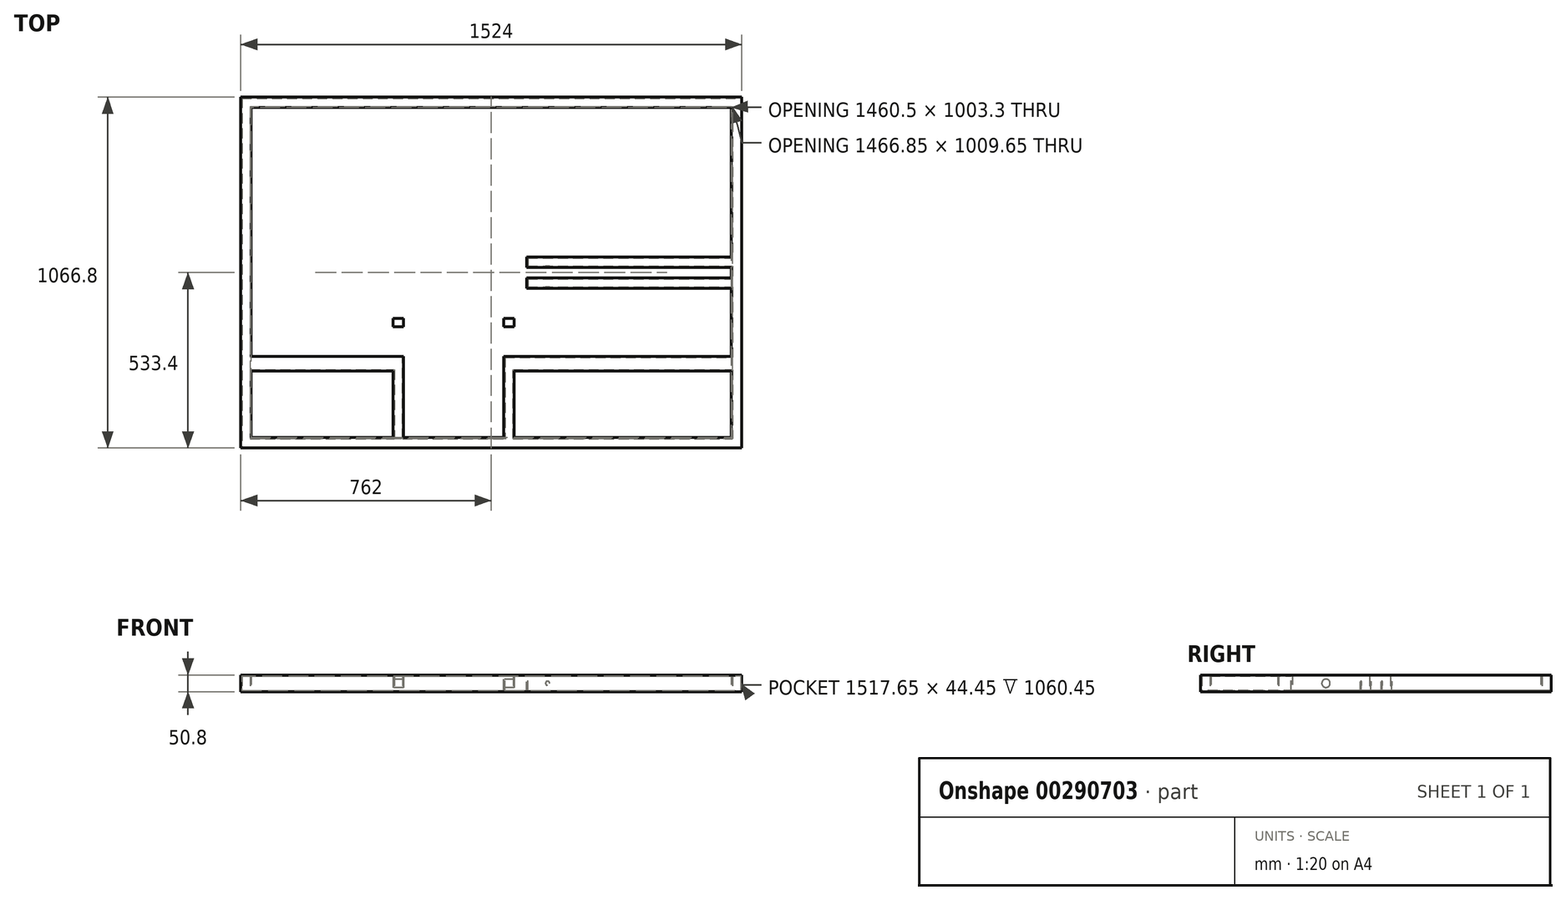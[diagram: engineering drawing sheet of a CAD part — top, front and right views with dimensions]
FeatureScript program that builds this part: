
annotation { "Feature Type Name" : "Feature", "Feature Type Description" : "" }
export const myFeature = defineFeature(function(context is Context, id is Id, definition is map)
    precondition{}
    {
        {
            var Q0;
            Q0=qCreatedBy(makeId("Top.planeOp"),FACE);
            var sketch = newSketch(context, id + "F0", { "sketchPlane" : qUnion([Q0])});
            skLineSegment(sketch, "E0.bottom", {"start": v(0, 0) * mm, "end": v(1524, 0) * mm});
            skLineSegment(sketch, "E0.top", {"start": v(0, -1066.8) * mm, "end": v(1524, -1066.8) * mm});
            skLineSegment(sketch, "E0.left", {"start": v(0, 0) * mm, "end": v(0, -1066.8) * mm});
            skLineSegment(sketch, "E0.right", {"start": v(1524, 0) * mm, "end": v(1524, -1066.8) * mm});
            skLineSegment(sketch, "E1.0", {"start": v(31.75, -31.75) * mm, "end": v(463.55, -31.75) * mm});
            skLineSegment(sketch, "E1.1", {"start": v(31.75, -31.75) * mm, "end": v(31.75, -1035.05) * mm});
            skLineSegment(sketch, "E1.2", {"start": v(31.75, -1035.05) * mm, "end": v(463.55, -1035.05) * mm});
            skLineSegment(sketch, "E1.3", {"start": v(1492.25, -31.75) * mm, "end": v(1492.25, -485.77) * mm});
            skLineSegment(sketch, "E2", {"start": v(463.55, -31.75) * mm, "end": v(463.55, -1035.05) * mm});
            skLineSegment(sketch, "E3", {"start": v(495.3, -1035.05) * mm, "end": v(495.3, -31.75) * mm});
            skLineSegment(sketch, "E4", {"start": v(800.1, -31.75) * mm, "end": v(800.1, -1035.05) * mm});
            skLineSegment(sketch, "E5", {"start": v(831.85, -1035.05) * mm, "end": v(831.85, -581.02) * mm});
            skLineSegment(sketch, "E6.trimOffspring", {"start": v(831.85, -1035.05) * mm, "end": v(1492.25, -1035.05) * mm});
            skLineSegment(sketch, "E7.trimOffspring", {"start": v(495.3, -1035.05) * mm, "end": v(800.1, -1035.05) * mm});
            skLineSegment(sketch, "E8.trimOffspring", {"start": v(495.3, -31.75) * mm, "end": v(800.1, -31.75) * mm});
            skLineSegment(sketch, "E9.trimOffspring", {"start": v(831.85, -31.75) * mm, "end": v(1492.25, -31.75) * mm});
            skLineSegment(sketch, "E10", {"start": v(31.75, -533.4) * mm, "end": v(2205.19, -533.4) * mm, "construction": true});
            skLineSegment(sketch, "E11.bottom", {"start": v(831.85, -517.52) * mm, "end": v(1492.25, -517.52) * mm});
            skLineSegment(sketch, "E11.top", {"start": v(831.85, -485.77) * mm, "end": v(1492.25, -485.77) * mm});
            skLineSegment(sketch, "E12.trimOffspring", {"start": v(831.85, -485.77) * mm, "end": v(831.85, -31.75) * mm});
            skLineSegment(sketch, "E13.trimOffspring", {"start": v(1492.25, -517.52) * mm, "end": v(1492.25, -549.27) * mm});
            skLineSegment(sketch, "E14.MirrorCS", {"start": v(831.85, -549.27) * mm, "end": v(1492.25, -549.27) * mm});
            skLineSegment(sketch, "E15.MirrorCS", {"start": v(831.85, -581.02) * mm, "end": v(1492.25, -581.02) * mm});
            skLineSegment(sketch, "E16.trimOffspring", {"start": v(831.85, -549.27) * mm, "end": v(831.85, -517.52) * mm});
            skLineSegment(sketch, "E17.trimOffspring", {"start": v(1492.25, -581.02) * mm, "end": v(1492.25, -1035.05) * mm});
            skLineSegment(sketch, "E18.bottom", {"start": v(31.75, -788.03) * mm, "end": v(463.55, -788.03) * mm});
            skLineSegment(sketch, "E18.top", {"start": v(31.75, -832.48) * mm, "end": v(463.55, -832.48) * mm});
            skLineSegment(sketch, "E18.left", {"start": v(31.75, -788.03) * mm, "end": v(31.75, -832.48) * mm});
            skLineSegment(sketch, "E18.right", {"start": v(463.55, -788.03) * mm, "end": v(463.55, -832.48) * mm});
            skLineSegment(sketch, "E19.bottom", {"start": v(831.85, -788.03) * mm, "end": v(1492.25, -788.03) * mm});
            skLineSegment(sketch, "E19.top", {"start": v(831.85, -832.48) * mm, "end": v(1492.25, -832.48) * mm});
            skLineSegment(sketch, "E19.left", {"start": v(831.85, -788.03) * mm, "end": v(831.85, -832.48) * mm});
            skLineSegment(sketch, "E19.right", {"start": v(1492.25, -788.03) * mm, "end": v(1492.25, -832.48) * mm});
            skSolve(sketch);
        }
        {
            var Q0;
            Q0=makeQuery(id+"F0.imprint","IMPRINT",FACE,{"disambiguationData":[TD([[makeQuery(id+"F0.imprint","IMPRINT",EDGE,{"derivedFrom":sQuery(id+"F0.wireOp",EDGE,"E0.bottom")}),-1.0]])]});
            var Q1;
            Q1=makeQuery(id+"F0.imprint","IMPRINT",FACE,{"disambiguationData":[TD([[makeQuery(id+"F0.imprint","IMPRINT",EDGE,{"derivedFrom":sQuery(id+"F0.wireOp",EDGE,"E18.bottom")}),-1.0]])]});
            var Q2;
            {var subQ0=sQuery(id+"F0.wireOp",EDGE,"d483128a-36f0-46c2-b19a-5627fc3941a30.MirrorCS");Q2=makeQuery(id+"F0.imprint","IMPRINT",FACE,{"disambiguationData":[TD([[makeQuery(id+"F0.imprint","IMPRINT",EDGE,{"derivedFrom":subQ0}),1.0]])]});}
            var Q3;
            {var subQ0=sQuery(id+"F0.wireOp",EDGE,"fc5f637f-702d-418a-97a0-bbe7b7dff5e80.MirrorCS");Q3=makeQuery(id+"F0.imprint","IMPRINT",FACE,{"disambiguationData":[TD([[makeQuery(id+"F0.imprint","IMPRINT",EDGE,{"derivedFrom":subQ0}),-1.0]])]});}
            var Q4;
            Q4=makeQuery(id+"F0.imprint","IMPRINT",FACE,{"disambiguationData":[TD([[makeQuery(id+"F0.imprint","IMPRINT",EDGE,{"derivedFrom":sQuery(id+"F0.wireOp",EDGE,"E19.bottom")}),-1.0]])]});
            extrude(context, id + "F1", {"entities" : qUnion([Q0, Q1, Q2, Q3, Q4]), "depth" : 50.8 * mm});
        }
        {
            var Q0;
            Q0=makeQuery(id+"F1.opExtrude","SWEPT_FACE",FACE,{"disambiguationData":[OSD([sQuery(id+"F0.wireOp",EDGE,"E2")])]});
            var sketch = newSketch(context, id + "F2", { "sketchPlane" : qUnion([Q0])});
            skLineSegment(sketch, "E20", {"start": v(31.75, 25.4) * mm, "end": v(1035.05, 25.4) * mm, "construction": true});
            skCircle(sketch, "E21", {"center": v(381, 25.4) * mm, "radius": 12.7 * mm});
            skPoint(sketch, "E22", {"position": v(533.4, 25.4) * mm});
            skLineSegment(sketch, "E23", {"start": v(533.4, 25.4) * mm, "end": v(533.4, 0) * mm, "construction": true});
            skCircle(sketch, "E24.MirrorC", {"center": v(685.8, 25.4) * mm, "radius": 12.7 * mm});
            skSolve(sketch);
        }
        {
            var Q0;
            Q0=makeQuery(id+"F2.imprint","IMPRINT",FACE,{"disambiguationData":[TD([[makeQuery(id+"F2.imprint","IMPRINT",EDGE,{"derivedFrom":sQuery(id+"F2.wireOp",EDGE,"E21")}),1.0]])]});
            var Q1;
            Q1=makeQuery(id+"F2.imprint","IMPRINT",FACE,{"disambiguationData":[TD([[makeQuery(id+"F2.imprint","IMPRINT",EDGE,{"derivedFrom":sQuery(id+"F2.wireOp",EDGE,"E24.MirrorC")}),-1.0]])]});
            extrude(context, id + "F3", {"entities" : qUnion([Q0, Q1]), "operationType" : NewBodyOperationType.REMOVE, "oppositeDirection" : true, "depth" : 406.4 * mm});
        }
        {
            var Q0;
            Q0=makeQuery(id+"F1.opExtrude","SWEPT_FACE",FACE,{"disambiguationData":[OSD([sQuery(id+"F0.wireOp",EDGE,"E11.top")])]});
            var sketch = newSketch(context, id + "F4", { "sketchPlane" : qUnion([Q0])});
            skLineSegment(sketch, "E25.0.0", {"start": v(-1492.25, 0) * mm, "end": v(-831.85, 0) * mm});
            skLineSegment(sketch, "E25.0.1", {"start": v(-831.85, 0) * mm, "end": v(-831.85, 50.8) * mm});
            skLineSegment(sketch, "E25.0.2", {"start": v(-831.85, 50.8) * mm, "end": v(-1492.25, 50.8) * mm});
            skLineSegment(sketch, "E25.0.3", {"start": v(-1492.25, 50.8) * mm, "end": v(-1492.25, 0) * mm});
            skCircle(sketch, "E26", {"center": v(-933.45, 25.4) * mm, "radius": 6.35 * mm});
            skPoint(sketch, "E26.centerSnap0", {"position": v(-831.85, 25.4) * mm});
            skSolve(sketch);
        }
        {
            var Q0;
            Q0=makeQuery(id+"F4.imprint","IMPRINT",FACE,{"disambiguationData":[TD([[makeQuery(id+"F4.imprint","IMPRINT",EDGE,{"derivedFrom":sQuery(id+"F4.wireOp",EDGE,"E26")}),1.0]])]});
            extrude(context, id + "F5", {"entities" : qUnion([Q0]), "operationType" : NewBodyOperationType.REMOVE, "oppositeDirection" : true, "depth" : 127 * mm});
        }
        {
            var Q0;
            Q0=makeQuery(id+"F3.boolean.opBoolean","COPY",FACE,{"disambiguationData":[TD([makeQuery(id+"F1.opExtrude","SWEPT_FACE",FACE,{"disambiguationData":[OSD([sQuery(id+"F0.wireOp",EDGE,"E4")])]})])],"derivedFrom":makeQuery(id+"F3.opExtrude","SWEPT_FACE",FACE,{"disambiguationData":[OSD([sQuery(id+"F2.wireOp",EDGE,"E21")])]})});
            var Q1;
            Q1=makeQuery(id+"F3.boolean.opBoolean","COPY",FACE,{"disambiguationData":[TD([makeQuery(id+"F1.opExtrude","SWEPT_FACE",FACE,{"disambiguationData":[OSD([sQuery(id+"F0.wireOp",EDGE,"E4")])]})])],"derivedFrom":makeQuery(id+"F3.opExtrude","SWEPT_FACE",FACE,{"disambiguationData":[OSD([sQuery(id+"F2.wireOp",EDGE,"f3b9bb93-9202-470c-8418-00dd5162cf0f0.MirrorC")])]})});
            var Q2;
            Q2=makeQuery(id+"F3.boolean.opBoolean","COPY",FACE,{"disambiguationData":[TD([makeQuery(id+"F1.opExtrude","SWEPT_FACE",FACE,{"disambiguationData":[OSD([sQuery(id+"F0.wireOp",EDGE,"E2")])]})])],"derivedFrom":makeQuery(id+"F3.opExtrude","SWEPT_FACE",FACE,{"disambiguationData":[OSD([sQuery(id+"F2.wireOp",EDGE,"E21")])]})});
            var Q3;
            Q3=makeQuery(id+"F3.boolean.opBoolean","COPY",FACE,{"disambiguationData":[TD([makeQuery(id+"F1.opExtrude","SWEPT_FACE",FACE,{"disambiguationData":[OSD([sQuery(id+"F0.wireOp",EDGE,"E2")])]})])],"derivedFrom":makeQuery(id+"F3.opExtrude","SWEPT_FACE",FACE,{"disambiguationData":[OSD([sQuery(id+"F2.wireOp",EDGE,"f3b9bb93-9202-470c-8418-00dd5162cf0f0.MirrorC")])]})});
            var Q4;
            Q4=makeQuery(id+"F5.boolean.opBoolean","COPY",FACE,{"disambiguationData":[TD([makeQuery(id+"F1.opExtrude","SWEPT_FACE",FACE,{"disambiguationData":[OSD([sQuery(id+"F0.wireOp",EDGE,"E14.MirrorCS")])]})])],"derivedFrom":makeQuery(id+"F5.opExtrude","SWEPT_FACE",FACE,{"disambiguationData":[OSD([sQuery(id+"F4.wireOp",EDGE,"E26")])]})});
            var Q5;
            Q5=makeQuery(id+"F5.boolean.opBoolean","COPY",FACE,{"disambiguationData":[TD([makeQuery(id+"F1.opExtrude","SWEPT_FACE",FACE,{"disambiguationData":[OSD([sQuery(id+"F0.wireOp",EDGE,"E11.bottom")])]})])],"derivedFrom":makeQuery(id+"F5.opExtrude","SWEPT_FACE",FACE,{"disambiguationData":[OSD([sQuery(id+"F4.wireOp",EDGE,"E26")])]})});
            shell(context, id + "F6", {"entities" : qUnion([Q0, Q1, Q2, Q3, Q4, Q5]), "thickness" : 3.17 * mm});
        }
    });
